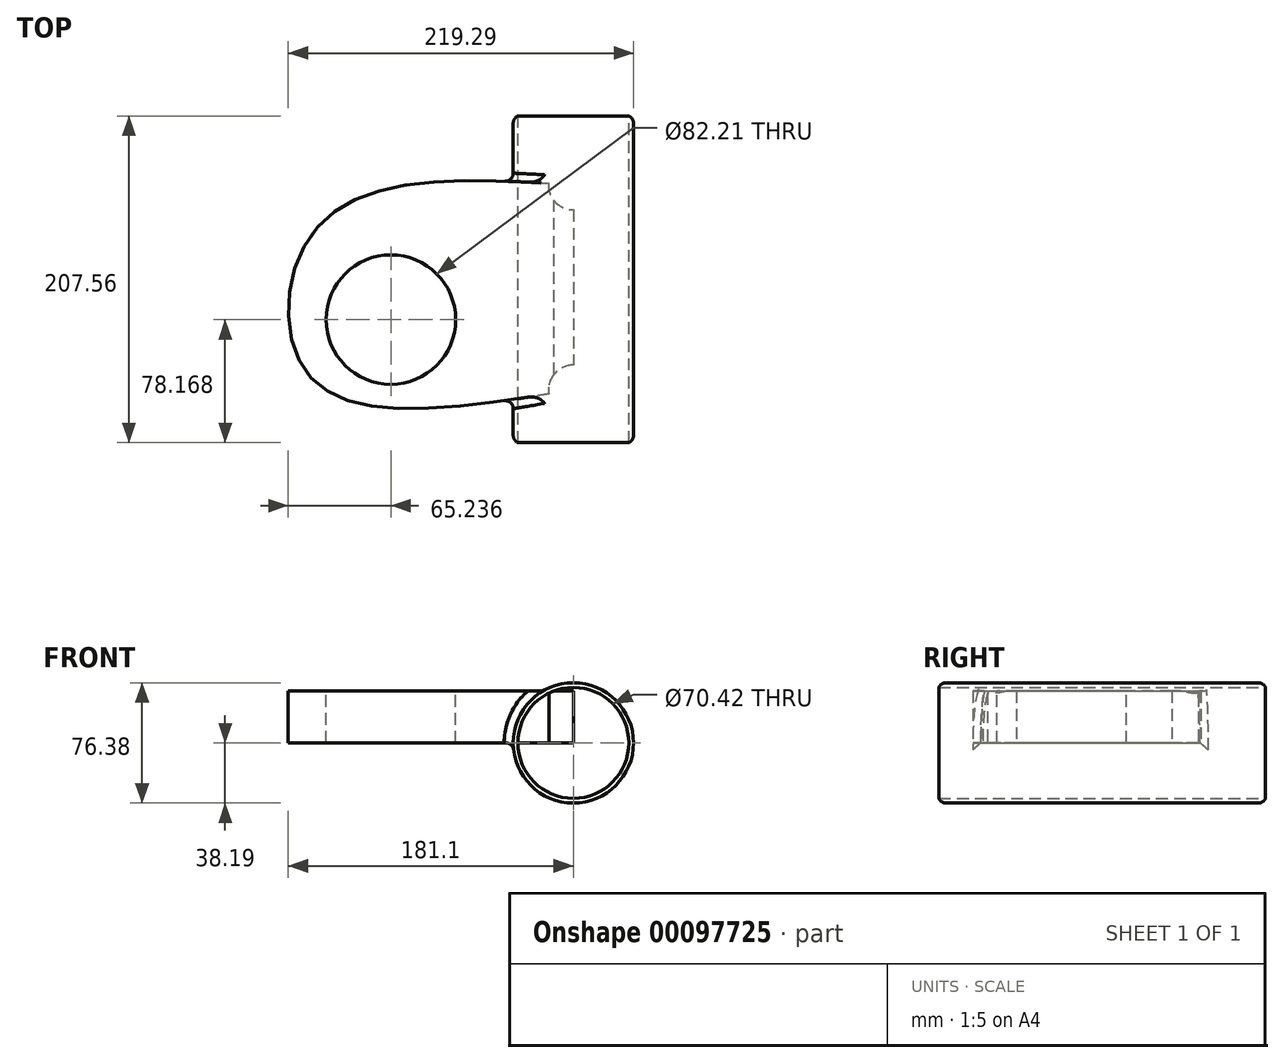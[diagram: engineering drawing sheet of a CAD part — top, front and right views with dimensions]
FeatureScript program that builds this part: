
annotation { "Feature Type Name" : "Feature", "Feature Type Description" : "" }
export const myFeature = defineFeature(function(context is Context, id is Id, definition is map)
    precondition{}
    {
        {
            var Q0;
            Q0=qCreatedBy(makeId("Front.planeOp"),FACE);
            var sketch = newSketch(context, id + "F0", { "sketchPlane" : qUnion([Q0])});
            skCircle(sketch, "E0", {"center": v(0, 0) * mm, "radius": 38.19 * mm});
            skCircle(sketch, "E1", {"center": v(0, 0) * mm, "radius": 35.21 * mm});
            skSolve(sketch);
        }
        {
            var Q0;
            Q0 = qSketchRegion(id + "F0", true);
            extrude(context, id + "F1", {"entities" : qUnion([Q0]), "depth" : 207.56 * mm});
        }
        {
            var Q0;
            Q0=qCreatedBy(makeId("Top.planeOp"),FACE);
            var sketch = newSketch(context, id + "F2", { "sketchPlane" : qUnion([Q0])});
            skCircle(sketch, "E2", {"center": v(0, -43.72) * mm, "radius": 15.9 * mm});
            skCircle(sketch, "E3", {"center": v(0, -174.05) * mm, "radius": 15.8 * mm});
            skLineSegment(sketch, "E4", {"start": v(15.9, -44.37) * mm, "end": v(38.33, -44.37) * mm});
            skLineSegment(sketch, "E5", {"start": v(0, -59.63) * mm, "end": v(0, -158.25) * mm});
            skLineSegment(sketch, "E6", {"start": v(0, -108.94) * mm, "end": v(-165.2, -108.94) * mm});
            skFitSpline(sketch, "E7", {"points": [v(0, -174.05) * mm, v(-166.88, -166.15) * mm, v(-161.35, -69.13) * mm, v(0, -43.72) * mm], "startDerivative": vector(-573.98, -94.06) * mm, "endDerivative": vector(545.37, -33.07) * mm});
            skSolve(sketch);
        }
        {
            var Q0;
            {var subQ0=sQuery(id+"F2.wireOp",EDGE,"E5");var subQ3=makeQuery(id+"F2.imprint","IMPRINT",VERTEX,{"derivedFrom":subQ0});Q0=makeQuery(id+"F2.imprint","IMPRINT",FACE,{"disambiguationData":[TD([[makeQuery(id+"F2.imprint","IMPRINT",EDGE,{"disambiguationData":[TD([[subQ3,1.0]])],"derivedFrom":subQ0}),-1.0]])]});}
            var Q1;
            Q1=sQuery(id+"F2.wireOp",EDGE,"E3");
            extrude(context, id + "F3", {"entities" : qUnion([Q0]), "operationType" : NewBodyOperationType.ADD, "surfaceEntities" : qUnion([Q1]), "depth" : 32.96 * mm});
        }
        {
            var Q0;
            Q0=qCreatedBy(makeId("Front.planeOp"),FACE);
            var sketch = newSketch(context, id + "F4", { "sketchPlane" : qUnion([Q0])});
            skCircle(sketch, "E8", {"center": v(0, 0) * mm, "radius": 34.55 * mm});
            skSolve(sketch);
        }
        {
            var Q0;
            Q0 = qSketchRegion(id + "F4", true);
            extrude(context, id + "F5", {"entities" : qUnion([Q0]), "operationType" : NewBodyOperationType.REMOVE, "endBound" : BoundingType.THROUGH_ALL, "oppositeDirection" : true, "depth" : 25.4 * mm});
        }
        {
            var Q0;
            {var subQ0=sQuery(id+"F2.wireOp",EDGE,"E7");Q0=makeQuery(id+"F3.boolean.opBoolean","SPLIT",FACE,{"disambiguationData":[TD([makeQuery(id+"F1.opExtrude","SWEPT_FACE",FACE,{"disambiguationData":[OSD([sQuery(id+"F0.wireOp",EDGE,"E0")])]})])],"derivedFrom":makeQuery(id+"F3.opExtrude","CAP_FACE",FACE,{"disambiguationData":[OSD([sQuery(id+"F2.wireOp",EDGE,"E2"),sQuery(id+"F2.wireOp",EDGE,"E3"),sQuery(id+"F2.wireOp",EDGE,"E5"),subQ0])],"isStart":false})});}
            var sketch = newSketch(context, id + "F6", { "sketchPlane" : qUnion([Q0])});
            skCircle(sketch, "E9", {"center": v(-115.86, -129.4) * mm, "radius": 41.1 * mm});
            skSolve(sketch);
        }
        {
            var Q0;
            Q0 = qSketchRegion(id + "F6", true);
            extrude(context, id + "F7", {"entities" : qUnion([Q0]), "operationType" : NewBodyOperationType.REMOVE, "endBound" : BoundingType.THROUGH_ALL, "oppositeDirection" : true, "depth" : 25.4 * mm});
        }
        {
            var Q0;
            Q0=makeQuery(id+"F1.opExtrude","SWEPT_FACE",FACE,{"disambiguationData":[OSD([sQuery(id+"F0.wireOp",EDGE,"E0")])]});
            fillet(context, id + "F8", {"entities" : qUnion([Q0]), "radius" : 5.08 * mm, "tangentPropagation" : true, "allowEdgeOverflow" : false});
        }
    });
